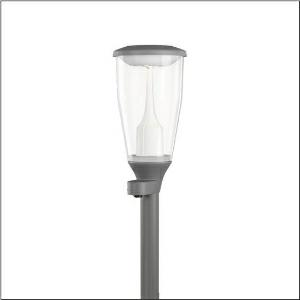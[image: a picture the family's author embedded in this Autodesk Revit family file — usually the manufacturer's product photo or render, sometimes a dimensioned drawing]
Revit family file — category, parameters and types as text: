
# Revit family: dl_11_iq___st1_2a_5xa5565eu14hp00022_7835
name_source: partatom
category: Lighting Fixtures
units: mm (PartAtom-declared; Revit-internal decimal feet)

## family parameters
Cut with Voids When Loaded = No
Host = Face
Light Source = No
Part Type = Normal
Room Calculation Point = No
Round Connector Dimension = Use Diameter
Shared = No

## types (1)
- --- (1 x LED, 4790 lm, 33.5 W, 3000K)
    Apparent Load = 34 VA
    CIE Flux Codes = 23 60 93 95 100
    Color Rendering = 70
    Color Temperature = 3000K
    Default Elevation = 1800 mm
    Description = DL 11 iQ, mast luminaire, Module 540 iQ-SR, primary light control with 3 zone facetted reflector, of plastic, silver coated, highly specular, structured, primary optical cover: cover, of PMMA, transparent, light distribution: ST1.2a, light emission: direct distribution, primary light characteristic: asymmetric, installation type: post-top, LED, High Power LED, rated luminous flux: 4.790lm, luminous efficacy: 143lm/W, light colour: 730, colour temperature: 3000K, control gear: iQ-Street Remote, D4i with power reduction, control: pre-setting: logarithmic dimming characteristic, Street-Remote, Auto-Match, Temp-Guard, Lumen-Switch, Night-Set, Smart-Wire, Light-Fading, Desk-Remote (wireless, voltage-free reading and setting of iQ features in the workshop via application-optimized NFC function/RFID function), optimised constant luminous flux control (CLO 2.0), mains connection: 220..240V, AC, 50/60Hz, connection cable pre-assembled, cable length: 5,5m, start of lifetime: 34W, end of service life: 36W, reduction: 15W, luminaire housing, upper part, of diecast aluminium, coated, SITECO metallic grey (DB 702S), spigot size: 60mm (post-top), mounting height: 3..5m, post-top mast mounting element, of diecast aluminium, coated, SITECO metallic grey (DB 702S), Module 540 iQ-SR, traffic white (RAL 9016), equipment: Power, Smart Interface below, protection rating (complete): IP66, insulation class (complete): insulation class II (safety insulation), certification: CE, ENEC, ENEC+, VDE, impact resistance: IK07, packaging unit: 1 piece

Light Distribution: ST1.2a
    Height = 665 mm
    Lamp = 1 x LED
    Lamp Light Flux = 4790 lm
    Lamp Power = 33.5 W
    Lamp count = 1
    Length = 334 mm
    Luminous efficacy = 143 lm/W
    Manufacturer = Siteco
    ModVariant = No
    Model = 5XA5565EU14HP00022
    Number of Poles = 1
    OnlyDefault = Yes
    Power Factor = 1
    Product Name = DL 11 iQ | ST1.2a
    Product group = mast luminaire | pylon top
    ProductGroupID = 6100
    Protection Class = Protection class II
    Protection Degree = IP 66
    RLX_Detail_Level = 1
    RLX_Emergency_Light_Flux = 0 lm
    RLX_Emergency_Type = 0
    RLX_Emergency_Type_DB = No
    RlxData = <blob elided: 161109 chars, md5=0ba83417>
    Socket = socket
    Standby Power = 0 W
    System Light Flux = 4790 lm
    System Power = 34 W
    Type Comments = factory setting: luminous flux: 100 % | dim-lin: 254 | 695 mA
    Type Image = l_1337539.jpg
    URL = http://relux.com
    VarID = @adj_040653
    Voltage = 0 V
    Weight = 0.00 kg
    Width = 0 mm  [stored 0 ft]

note: [stored X ft] marks values corroborated as IEEE doubles in the binary element streams (Revit-internal decimal feet)

## geometry (parser evidence)
native form markers: Blend x4, Sweep x14
no freeform markers — native parametric forms only
